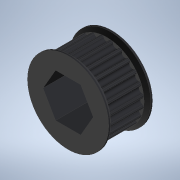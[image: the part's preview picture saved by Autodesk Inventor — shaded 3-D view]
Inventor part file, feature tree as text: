
AUTODESK INVENTOR PART (.ipt)
format: ipt  version: 2022.3 (Build 263350000, 350)  size: 311,808 bytes
history: native  units: in
note: dims shown in document units (in); Inventor stores cm internally (conversion verified against a paired STEP export)
features: extrude x7, sketch x7, fillet x2, pattern_circular x2, mirror x2, chamfer x2, other x1
ambient origin geometry x8: Origin, YZ Plane, XZ Plane, XY Plane, X Axis, Y Axis, Z Axis, Center Point
bodies: Solid1 (feature_tree)
feature tree (23):
  other  "Hex Bore"
  extrude  "HTD Base"  Depth=0.3937in TaperAngle=0.0deg
  extrude  "HTD Base Tooth"  Depth=0.0113in
  fillet  "HTD Base Tooth pt. 2"  [1 undecoded]
  pattern_circular  "HTD Teeth"  Count=24  [1 undecoded]
  extrude  "HTD Flange"  Depth=0.0394in
  mirror  "HTD Flanges"
  chamfer  "HTD Flange Chamfer"  Distance=0.0787in Angle=45.0deg
  extrude  "GT2 Base"  Depth=0.51in
  extrude  "GT2 Base Tooth"  TaperAngle=0.0deg  [1 undecoded]
  fillet  "GT2 Base Tooth pt. 2"  Radius=0.51in
  pattern_circular  "GT2 Teeth"  [2 undecoded]
  extrude  "GT2 Flange"  Depth=0.0591in
  mirror  "GT2 Flanges"
  chamfer  "GT2 Flange Chamfer"  Distance=0.3937in
  extrude  "Circle Bore"  TaperAngle=0.0deg  [1 undecoded]
  sketch  "Sketch1"  dims[d0=1.4588in d1=0.3937in d2=0.0in]
  sketch  "Sketch2"  dims[d3=0.1208in d5=0.0113in d6=0.0in d7=0.0in]
  sketch  "Sketch3"  dims[d8=0.0169in d9=9.4488in]
  sketch  "Sketch4"  dims[d10=360.0deg d12=0.0394in]
  sketch  "Sketch5"  dims[d13=0.0591in]
  sketch  "Sketch6"  dims[d14=0.0in]
  sketch  "Sketch7"  dims[d15=0.0394in d16=0.0787in d17=45.0deg d18=0.51in d19=0.0in d20=0.0in d21=0.51in d22=0.0in d23=0.0in d24=0.8723in d25=0.3937in d26=0.0in d27=0.0727in d28=0.0075in d29=0.0in d30=0.0in d31=0.0118in d32=9.4488in d33=360.0deg d35=0.0394in d36=0.0591in d37=0.0in d38=0.0394in d39=0.0787in d40=45.0deg]
note: 6 required parameter values undecoded (feature->parameter linkage not recoverable at this tier; creation-order binding heuristic only, values carry confidence <= 0.55)
